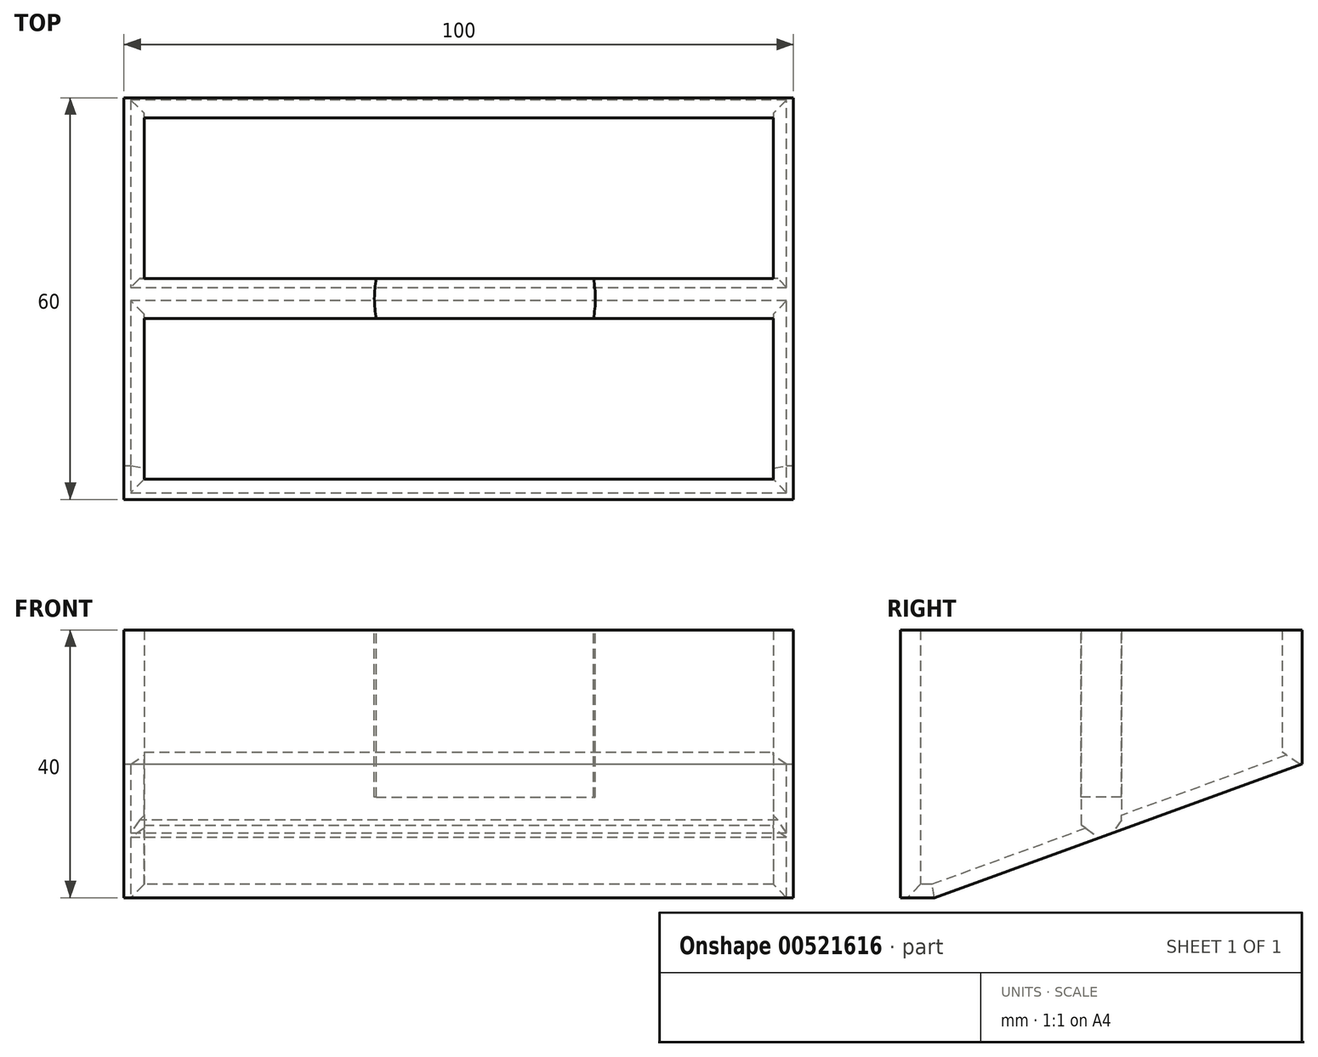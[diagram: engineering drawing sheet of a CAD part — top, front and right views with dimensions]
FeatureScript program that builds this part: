
annotation { "Feature Type Name" : "Feature", "Feature Type Description" : "" }
export const myFeature = defineFeature(function(context is Context, id is Id, definition is map)
    precondition{}
    {
        {
            var Q0;
            Q0=qCreatedBy(makeId("Top.planeOp"),FACE);
            var sketch = newSketch(context, id + "F0", { "sketchPlane" : qUnion([Q0])});
            skLineSegment(sketch, "E0.bottom", {"start": v(50, -30) * mm, "end": v(-50, -30) * mm});
            skLineSegment(sketch, "E0.top", {"start": v(50, 30) * mm, "end": v(-50, 30) * mm});
            skLineSegment(sketch, "E0.left", {"start": v(50, -30) * mm, "end": v(50, 30) * mm});
            skLineSegment(sketch, "E0.right", {"start": v(-50, -30) * mm, "end": v(-50, 30) * mm});
            skPoint(sketch, "E0.middle", {"position": v(0, 0) * mm});
            skLineSegment(sketch, "E1", {"start": v(-50, 0) * mm, "end": v(50, 0) * mm});
            skPoint(sketch, "E2.endSnap0", {"position": v(0, 30) * mm});
            skLineSegment(sketch, "E3", {"start": v(-50, 0) * mm, "end": v(-47, 0) * mm});
            skLineSegment(sketch, "E4", {"start": v(50, 0) * mm, "end": v(47, 0) * mm});
            skLineSegment(sketch, "E5", {"start": v(-47, 27) * mm, "end": v(47, 27) * mm});
            skLineSegment(sketch, "E6", {"start": v(47, 27) * mm, "end": v(47, -27) * mm});
            skLineSegment(sketch, "E7", {"start": v(47, -27) * mm, "end": v(-47, -27) * mm});
            skLineSegment(sketch, "E8", {"start": v(-47, -3) * mm, "end": v(47, -3) * mm});
            skLineSegment(sketch, "E9", {"start": v(-47, 3) * mm, "end": v(47, 3) * mm});
            skLineSegment(sketch, "E10", {"start": v(-47, 27) * mm, "end": v(-47, 3) * mm});
            skLineSegment(sketch, "E11", {"start": v(-47, -3) * mm, "end": v(-47, -27) * mm});
            skSolve(sketch);
        }
        {
            var Q0;
            Q0=makeQuery(id+"F0.imprint","IMPRINT",FACE,{"disambiguationData":[TD([[makeQuery(id+"F0.imprint","IMPRINT",EDGE,{"derivedFrom":sQuery(id+"F0.wireOp",EDGE,"E0.bottom")}),-1.0]])]});
            var Q1;
            {var subQ1=sQuery(id+"F0.wireOp",EDGE,"E2");Q1=makeQuery(id+"F0.imprint","IMPRINT",FACE,{"disambiguationData":[TD([[makeQuery(id+"F0.imprint","IMPRINT",EDGE,{"derivedFrom":subQ1}),-1.0]])]});}
            var Q2;
            {var subQ0=sQuery(id+"F0.wireOp",EDGE,"E2");Q2=makeQuery(id+"F0.imprint","IMPRINT",FACE,{"disambiguationData":[TD([[makeQuery(id+"F0.imprint","IMPRINT",EDGE,{"derivedFrom":subQ0}),1.0]])]});}
            var Q3;
            {var subQ1=sQuery(id+"F0.wireOp",EDGE,"E0.top");Q3=makeQuery(id+"F0.imprint","IMPRINT",FACE,{"disambiguationData":[TD([[makeQuery(id+"F0.imprint","IMPRINT",EDGE,{"derivedFrom":subQ1}),1.0]])]});}
            extrude(context, id + "F1", {"entities" : qUnion([Q0, Q1, Q2, Q3]), "depth" : 40 * mm, "offsetDistance" : 25 * mm});
        }
        {
            var Q0;
            Q0=makeQuery(id+"F1.opExtrude","SWEPT_FACE",FACE,{"disambiguationData":[OSD([sQuery(id+"F0.wireOp",EDGE,"E0.left")])]});
            var sketch = newSketch(context, id + "F2", { "sketchPlane" : qUnion([Q0])});
            skLineSegment(sketch, "E12", {"start": v(30, 20) * mm, "end": v(-24.95, 0) * mm});
            skSolve(sketch);
        }
        {
            var Q0;
            {var subQ0=sQuery(id+"F2.wireOp",EDGE,"E12");Q0=makeQuery(id+"F2.imprint","IMPRINT",FACE,{"disambiguationData":[TD([[makeQuery(id+"F2.imprint","IMPRINT",EDGE,{"derivedFrom":subQ0}),1.0]])]});}
            extrude(context, id + "F3", {"entities" : qUnion([Q0]), "operationType" : NewBodyOperationType.REMOVE, "endBound" : BoundingType.THROUGH_ALL, "oppositeDirection" : true, "depth" : 25 * mm, "offsetDistance" : 25 * mm});
        }
        {
            var Q0;
            Q0=makeQuery(id+"F1.opExtrude","CAP_EDGE",EDGE,{"disambiguationData":[OSD([sQuery(id+"F0.wireOp",EDGE,"E7")])],"isStart":true});
            var Q1;
            Q1=makeQuery(id+"F3.boolean.opBoolean","INTERSECT",EDGE,{"derivedFrom":[makeQuery(id+"F1.opExtrude","SWEPT_FACE",FACE,{"disambiguationData":[OSD([sQuery(id+"F0.wireOp",EDGE,"E8")])]}),makeQuery(id+"F3.opExtrude","SWEPT_FACE",FACE,{"disambiguationData":[OSD([sQuery(id+"F2.wireOp",EDGE,"E12")])]})]});
            var Q2;
            Q2=makeQuery(id+"F3.boolean.opBoolean","INTERSECT",EDGE,{"derivedFrom":[makeQuery(id+"F1.opExtrude","SWEPT_FACE",FACE,{"disambiguationData":[OSD([sQuery(id+"F0.wireOp",EDGE,"E11")])]}),makeQuery(id+"F3.opExtrude","SWEPT_FACE",FACE,{"disambiguationData":[OSD([sQuery(id+"F2.wireOp",EDGE,"E12")])]})]});
            var Q3;
            {var subQ0=sQuery(id+"F0.wireOp",EDGE,"E6");Q3=makeQuery(id+"F3.boolean.opBoolean","INTERSECT",EDGE,{"derivedFrom":[makeQuery(id+"F1.opExtrude","SWEPT_FACE",FACE,{"disambiguationData":[OSD([subQ0]),TDD([makeQuery(id+"F0.imprint","IMPRINT",EDGE,{"disambiguationData":[TD([[makeQuery(id+"F0.imprint","INTERSECT",VERTEX,{"derivedFrom":[subQ0,sQuery(id+"F0.wireOp",EDGE,"E7")]}),1.0]])],"derivedFrom":subQ0})])]}),makeQuery(id+"F3.opExtrude","SWEPT_FACE",FACE,{"disambiguationData":[OSD([sQuery(id+"F2.wireOp",EDGE,"E12")])]})]});}
            var Q4;
            {var subQ0=sQuery(id+"F0.wireOp",EDGE,"E6");Q4=makeQuery(id+"F3.boolean.opBoolean","INTERSECT",EDGE,{"derivedFrom":[makeQuery(id+"F1.opExtrude","SWEPT_FACE",FACE,{"disambiguationData":[OSD([subQ0]),TDD([makeQuery(id+"F0.imprint","IMPRINT",EDGE,{"disambiguationData":[TD([[makeQuery(id+"F0.imprint","INTERSECT",VERTEX,{"derivedFrom":[sQuery(id+"F0.wireOp",EDGE,"E5"),subQ0]}),-1.0]])],"derivedFrom":subQ0})])]}),makeQuery(id+"F3.opExtrude","SWEPT_FACE",FACE,{"disambiguationData":[OSD([sQuery(id+"F2.wireOp",EDGE,"E12")])]})]});}
            var Q5;
            Q5=makeQuery(id+"F3.boolean.opBoolean","INTERSECT",EDGE,{"derivedFrom":[makeQuery(id+"F1.opExtrude","SWEPT_FACE",FACE,{"disambiguationData":[OSD([sQuery(id+"F0.wireOp",EDGE,"E9")])]}),makeQuery(id+"F3.opExtrude","SWEPT_FACE",FACE,{"disambiguationData":[OSD([sQuery(id+"F2.wireOp",EDGE,"E12")])]})]});
            var Q6;
            Q6=makeQuery(id+"F3.boolean.opBoolean","INTERSECT",EDGE,{"derivedFrom":[makeQuery(id+"F1.opExtrude","SWEPT_FACE",FACE,{"disambiguationData":[OSD([sQuery(id+"F0.wireOp",EDGE,"E10")])]}),makeQuery(id+"F3.opExtrude","SWEPT_FACE",FACE,{"disambiguationData":[OSD([sQuery(id+"F2.wireOp",EDGE,"E12")])]})]});
            var Q7;
            Q7=makeQuery(id+"F3.boolean.opBoolean","INTERSECT",EDGE,{"derivedFrom":[makeQuery(id+"F1.opExtrude","SWEPT_FACE",FACE,{"disambiguationData":[OSD([sQuery(id+"F0.wireOp",EDGE,"E5")])]}),makeQuery(id+"F3.opExtrude","SWEPT_FACE",FACE,{"disambiguationData":[OSD([sQuery(id+"F2.wireOp",EDGE,"E12")])]})]});
            var Q8;
            {var subQ0=sQuery(id+"F0.wireOp",EDGE,"E6");Q8=makeQuery(id+"F1.opExtrude","CAP_EDGE",EDGE,{"disambiguationData":[OSD([subQ0]),TDD([makeQuery(id+"F0.imprint","IMPRINT",EDGE,{"disambiguationData":[TD([[makeQuery(id+"F0.imprint","INTERSECT",VERTEX,{"derivedFrom":[subQ0,sQuery(id+"F0.wireOp",EDGE,"E7")]}),1.0]])],"derivedFrom":subQ0})])],"isStart":true});}
            var Q9;
            Q9=makeQuery(id+"F1.opExtrude","CAP_EDGE",EDGE,{"disambiguationData":[OSD([sQuery(id+"F0.wireOp",EDGE,"E11")])],"isStart":true});
            chamfer(context, id + "F4", {"entities" : qUnion([Q0, Q1, Q2, Q3, Q4, Q5, Q6, Q7, Q8, Q9]), "width" : 2 * mm, "tangentPropagation" : true});
        }
        {
            var Q0;
            Q0=makeQuery(id+"F1.opExtrude","CAP_FACE",FACE,{"disambiguationData":[OSD([sQuery(id+"F0.wireOp",EDGE,"E0.bottom"),sQuery(id+"F0.wireOp",EDGE,"E0.top"),sQuery(id+"F0.wireOp",EDGE,"E0.left"),sQuery(id+"F0.wireOp",EDGE,"E0.right"),sQuery(id+"F0.wireOp",EDGE,"E5"),sQuery(id+"F0.wireOp",EDGE,"E6"),sQuery(id+"F0.wireOp",EDGE,"E7"),sQuery(id+"F0.wireOp",EDGE,"E8"),sQuery(id+"F0.wireOp",EDGE,"E9"),sQuery(id+"F0.wireOp",EDGE,"E10"),sQuery(id+"F0.wireOp",EDGE,"E11")])],"isStart":false});
            var sketch = newSketch(context, id + "F5", { "sketchPlane" : qUnion([Q0])});
            skCircle(sketch, "E13", {"center": v(3.91, 0) * mm, "radius": 16.5 * mm});
            skLineSegment(sketch, "E14", {"start": v(20.41, 0) * mm, "end": v(-12.59, 0) * mm});
            skLineSegment(sketch, "E15", {"start": v(3.91, 0) * mm, "end": v(3.91, -1.5) * mm});
            skLineSegment(sketch, "E16", {"start": v(3.91, 0) * mm, "end": v(3.91, 1.5) * mm});
            skLineSegment(sketch, "E17", {"start": v(20.34, 1.5) * mm, "end": v(-12.52, 1.5) * mm});
            skLineSegment(sketch, "E18", {"start": v(20.34, -1.5) * mm, "end": v(-12.52, -1.5) * mm});
            skSolve(sketch);
        }
        {
            var Q0;
            {var subQ0=sQuery(id+"F5.wireOp",EDGE,"E13");var subQ1=makeQuery(id+"F1.opExtrude","CAP_EDGE",EDGE,{"disambiguationData":[OSD([sQuery(id+"F0.wireOp",EDGE,"E9")])],"isStart":false});var subQ2=makeQuery(id+"F5.imprint","INTERSECT",VERTEX,{"disambiguationData":[OD(0.0)],"derivedFrom":[subQ1,subQ0]});Q0=makeQuery(id+"F5.imprint","IMPRINT",FACE,{"disambiguationData":[TD([[makeQuery(id+"F5.imprint","IMPRINT",EDGE,{"disambiguationData":[TD([[subQ2,-1.0]])],"derivedFrom":subQ0}),1.0]])]});}
            var Q1;
            {var subQ0=sQuery(id+"F5.wireOp",EDGE,"E18");var subQ2=sQuery(id+"F5.wireOp",EDGE,"E13");var subQ3=makeQuery(id+"F5.imprint","INTERSECT",VERTEX,{"disambiguationData":[OD(1.0)],"derivedFrom":[subQ2,subQ0]});Q1=makeQuery(id+"F5.imprint","IMPRINT",FACE,{"disambiguationData":[TD([[makeQuery(id+"F5.imprint","IMPRINT",EDGE,{"disambiguationData":[TD([[subQ3,-1.0]])],"derivedFrom":subQ2}),1.0]])]});}
            var Q2;
            {var subQ0=sQuery(id+"F5.wireOp",EDGE,"E17");var subQ2=sQuery(id+"F5.wireOp",EDGE,"E13");var subQ4=makeQuery(id+"F5.imprint","INTERSECT",VERTEX,{"disambiguationData":[OD(0.0)],"derivedFrom":[subQ2,subQ0]});Q2=makeQuery(id+"F5.imprint","IMPRINT",FACE,{"disambiguationData":[TD([[makeQuery(id+"F5.imprint","IMPRINT",EDGE,{"disambiguationData":[TD([[subQ4,-1.0]])],"derivedFrom":subQ2}),1.0]])]});}
            var Q3;
            {var subQ5=sQuery(id+"F5.wireOp",EDGE,"E16");Q3=makeQuery(id+"F5.imprint","IMPRINT",FACE,{"disambiguationData":[TD([[makeQuery(id+"F5.imprint","IMPRINT",EDGE,{"derivedFrom":subQ5}),-1.0]])]});}
            var Q4;
            {var subQ5=sQuery(id+"F5.wireOp",EDGE,"E15");Q4=makeQuery(id+"F5.imprint","IMPRINT",FACE,{"disambiguationData":[TD([[makeQuery(id+"F5.imprint","IMPRINT",EDGE,{"derivedFrom":subQ5}),1.0]])]});}
            var Q5;
            {var subQ5=sQuery(id+"F5.wireOp",EDGE,"E15");Q5=makeQuery(id+"F5.imprint","IMPRINT",FACE,{"disambiguationData":[TD([[makeQuery(id+"F5.imprint","IMPRINT",EDGE,{"derivedFrom":subQ5}),-1.0]])]});}
            var Q6;
            {var subQ5=sQuery(id+"F5.wireOp",EDGE,"E16");Q6=makeQuery(id+"F5.imprint","IMPRINT",FACE,{"disambiguationData":[TD([[makeQuery(id+"F5.imprint","IMPRINT",EDGE,{"derivedFrom":subQ5}),1.0]])]});}
            extrude(context, id + "F6", {"entities" : qUnion([Q0, Q1, Q2, Q3, Q4, Q5, Q6]), "operationType" : NewBodyOperationType.REMOVE, "oppositeDirection" : true, "depth" : 25 * mm, "offsetDistance" : 25 * mm});
        }
    });
